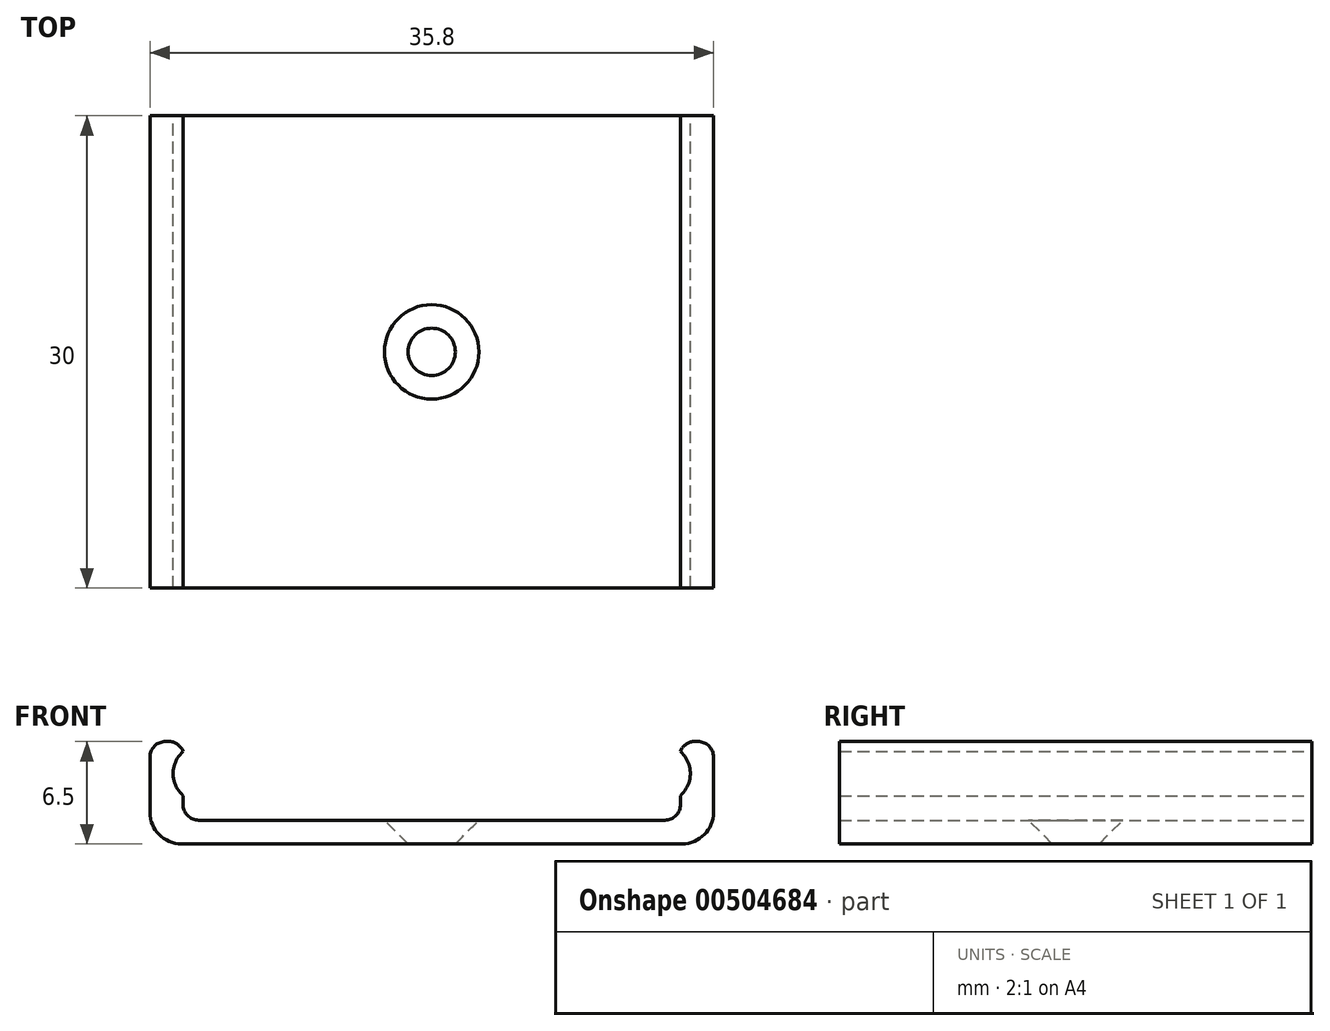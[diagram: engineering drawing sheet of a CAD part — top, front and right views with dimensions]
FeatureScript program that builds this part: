
annotation { "Feature Type Name" : "Feature", "Feature Type Description" : "" }
export const myFeature = defineFeature(function(context is Context, id is Id, definition is map)
    precondition{}
    {
        {
            var Q0;
            Q0=qCreatedBy(makeId("Front.planeOp"),FACE);
            var sketch = newSketch(context, id + "F0", { "sketchPlane" : qUnion([Q0])});
            skLineSegment(sketch, "E0", {"start": v(-17.9, 0) * mm, "end": v(17.9, 0) * mm});
            skLineSegment(sketch, "E1", {"start": v(-16.4, 15.5) * mm, "end": v(-16.4, -15.28) * mm, "construction": true});
            skLineSegment(sketch, "E2", {"start": v(16.4, 15.5) * mm, "end": v(16.4, -15.28) * mm, "construction": true});
            skLineSegment(sketch, "E3", {"start": v(15.8, 1.5) * mm, "end": v(8, 1.5) * mm});
            skLineSegment(sketch, "E4", {"start": v(0, 15.5) * mm, "end": v(0, -15.28) * mm, "construction": true});
            skLineSegment(sketch, "E5.trimOffspring", {"start": v(-8, 1.5) * mm, "end": v(-15.8, 1.5) * mm});
            skLineSegment(sketch, "E6", {"start": v(-17.9, 6.5) * mm, "end": v(-15.8, 6.5) * mm});
            skLineSegment(sketch, "E7", {"start": v(-15.8, 6.5) * mm, "end": v(-15.8, 1.5) * mm});
            skLineSegment(sketch, "E8", {"start": v(17.9, 6.5) * mm, "end": v(15.8, 6.5) * mm});
            skLineSegment(sketch, "E9", {"start": v(15.8, 6.5) * mm, "end": v(15.8, 1.5) * mm});
            skLineSegment(sketch, "E10", {"start": v(17.9, 6.5) * mm, "end": v(17.9, 0) * mm});
            skLineSegment(sketch, "E11", {"start": v(-17.9, 6.5) * mm, "end": v(-17.9, 0) * mm});
            skEllipse(sketch, "E12", {"center": v(12.93, 4.47) * mm, "majorRadius": 3.5 * mm, "minorRadius": 2.48 * mm, "majorAxis": v(-1, 0)});
            skEllipse(sketch, "E13", {"center": v(-12.93, 4.47) * mm, "majorRadius": 3.5 * mm, "minorRadius": 2.48 * mm, "majorAxis": v(-1, 0)});
            skLineSegment(sketch, "E14", {"start": v(-8, 1.5) * mm, "end": v(8, 1.5) * mm});
            skSolve(sketch);
        }
        {
            var Q0;
            Q0=qSketchRegion(id+"F0",true);
            extrude(context, id + "F1", {"entities" : qUnion([Q0]), "depth" : 30 * mm});
        }
        {
            var Q0;
            Q0=makeQuery(id+"F1.opExtrude","SWEPT_FACE",FACE,{"disambiguationData":[OSD([sQuery(id+"F0.wireOp",EDGE,"E3"),sQuery(id+"F0.wireOp",EDGE,"E5.trimOffspring"),sQuery(id+"F0.wireOp",EDGE,"E14")])]});
            var sketch = newSketch(context, id + "F2", { "sketchPlane" : qUnion([Q0])});
            skLineSegment(sketch, "E15", {"start": v(0, -30) * mm, "end": v(0, 0) * mm, "construction": true});
            skLineSegment(sketch, "E16", {"start": v(15.8, -15) * mm, "end": v(-15.8, -15) * mm, "construction": true});
            skCircle(sketch, "E17", {"center": v(0, -15) * mm, "radius": 3 * mm});
            skSolve(sketch);
        }
        {
            var Q0;
            Q0=sQuery(id+"F2.wireOp",VERTEX,"E17.center");
            var Q1;
            Q1=makeQuery(id+"F1.opExtrude","SWEPT_BODY",BODY,{"disambiguationData":[OSD([sQuery(id+"F0.wireOp",EDGE,"E0"),sQuery(id+"F0.wireOp",EDGE,"E3"),sQuery(id+"F0.wireOp",EDGE,"D1xSTUMQ-20cp-QuWq-AnQI-jtTS1Aydl4wU"),sQuery(id+"F0.wireOp",EDGE,"RWH1BVH5-31CH-0wRi-MlRQ-n6gno6U9d2sJ"),sQuery(id+"F0.wireOp",EDGE,"HIeZi0eG-o20j-5PzK-DNVY-zvFXTWfz9iDB"),sQuery(id+"F0.wireOp",EDGE,"E5.trimOffspring"),sQuery(id+"F0.wireOp",EDGE,"E6"),sQuery(id+"F0.wireOp",EDGE,"E7"),sQuery(id+"F0.wireOp",EDGE,"E8"),sQuery(id+"F0.wireOp",EDGE,"E9"),sQuery(id+"F0.wireOp",EDGE,"E10"),sQuery(id+"F0.wireOp",EDGE,"E11")])]});
            hole(context, id + "F3", {"style" : HoleStyle.C_SINK, "endStyle" : HoleEndStyle.THROUGH, "holeDiameter" : 3 * mm, "cSinkDiameter" : 6 * mm, "cSinkAngle" : 90 * degree, "isTappedThrough" : true, "tappedDepth" : 12 * mm, "tapClearance" : 3, "locations" : qUnion([Q0]), "scope" : qUnion([Q1]), "majorDiameter" : 5 * mm});
        }
        {
            var Q0;
            {var subQ0=sQuery(id+"F0.wireOp",EDGE,"E12");var subQ1=sQuery(id+"F0.wireOp",EDGE,"E9");var subQ2=makeQuery(id+"F0.imprint","INTERSECT",VERTEX,{"disambiguationData":[OD(0.0)],"derivedFrom":[subQ1,subQ0]});Q0=makeQuery(id+"F0.imprint","IMPRINT",FACE,{"disambiguationData":[TD([[makeQuery(id+"F0.imprint","IMPRINT",EDGE,{"disambiguationData":[TD([[subQ2,-1.0]])],"derivedFrom":subQ1}),-1.0]])]});}
            var Q1;
            {var subQ0=sQuery(id+"F0.wireOp",EDGE,"E12");var subQ1=sQuery(id+"F0.wireOp",EDGE,"E9");var subQ2=makeQuery(id+"F0.imprint","INTERSECT",VERTEX,{"disambiguationData":[OD(0.0)],"derivedFrom":[subQ1,subQ0]});Q1=makeQuery(id+"F0.imprint","IMPRINT",FACE,{"disambiguationData":[TD([[makeQuery(id+"F0.imprint","IMPRINT",EDGE,{"disambiguationData":[TD([[subQ2,-1.0]])],"derivedFrom":subQ1}),1.0]])]});}
            var Q2;
            {var subQ0=sQuery(id+"F0.wireOp",EDGE,"E13");var subQ1=sQuery(id+"F0.wireOp",EDGE,"E7");var subQ2=makeQuery(id+"F0.imprint","INTERSECT",VERTEX,{"disambiguationData":[OD(0.0)],"derivedFrom":[subQ1,subQ0]});Q2=makeQuery(id+"F0.imprint","IMPRINT",FACE,{"disambiguationData":[TD([[makeQuery(id+"F0.imprint","IMPRINT",EDGE,{"disambiguationData":[TD([[subQ2,-1.0]])],"derivedFrom":subQ1}),1.0]])]});}
            var Q3;
            {var subQ0=sQuery(id+"F0.wireOp",EDGE,"E13");var subQ1=sQuery(id+"F0.wireOp",EDGE,"E7");var subQ2=makeQuery(id+"F0.imprint","INTERSECT",VERTEX,{"disambiguationData":[OD(0.0)],"derivedFrom":[subQ1,subQ0]});Q3=makeQuery(id+"F0.imprint","IMPRINT",FACE,{"disambiguationData":[TD([[makeQuery(id+"F0.imprint","IMPRINT",EDGE,{"disambiguationData":[TD([[subQ2,-1.0]])],"derivedFrom":subQ1}),-1.0]])]});}
            var Q4;
            Q4=sQuery(id+"F0.wireOp",EDGE,"E12");
            extrude(context, id + "F4", {"entities" : qUnion([Q0, Q1, Q2, Q3]), "operationType" : NewBodyOperationType.REMOVE, "surfaceEntities" : qUnion([Q4]), "endBound" : BoundingType.THROUGH_ALL, "depth" : 25 * mm});
        }
        {
            var Q0;
            Q0=makeQuery(id+"F1.opExtrude","SWEPT_EDGE",EDGE,{"disambiguationData":[OSD([sQuery(id+"F0.wireOp",EDGE,"E6"),sQuery(id+"F0.wireOp",EDGE,"E11")])]});
            var Q1;
            Q1=makeQuery(id+"F1.opExtrude","SWEPT_EDGE",EDGE,{"disambiguationData":[OSD([sQuery(id+"F0.wireOp",EDGE,"E8"),sQuery(id+"F0.wireOp",EDGE,"E10")])]});
            var Q2;
            Q2=makeQuery(id+"F1.opExtrude","SWEPT_EDGE",EDGE,{"disambiguationData":[OSD([sQuery(id+"F0.wireOp",EDGE,"E6"),sQuery(id+"F0.wireOp",EDGE,"E7")])]});
            var Q3;
            Q3=makeQuery(id+"F1.opExtrude","SWEPT_EDGE",EDGE,{"disambiguationData":[OSD([sQuery(id+"F0.wireOp",EDGE,"E8"),sQuery(id+"F0.wireOp",EDGE,"E9")])]});
            fillet(context, id + "F5", {"entities" : qUnion([Q0, Q1, Q2, Q3]), "radius" : 1 * mm, "tangentPropagation" : true, "allowEdgeOverflow" : false});
        }
        {
            var Q0;
            Q0=makeQuery(id+"F1.opExtrude","SWEPT_EDGE",EDGE,{"disambiguationData":[OSD([sQuery(id+"F0.wireOp",EDGE,"E5.trimOffspring"),sQuery(id+"F0.wireOp",EDGE,"E7")])]});
            var Q1;
            Q1=makeQuery(id+"F1.opExtrude","SWEPT_EDGE",EDGE,{"disambiguationData":[OSD([sQuery(id+"F0.wireOp",EDGE,"E3"),sQuery(id+"F0.wireOp",EDGE,"E9")])]});
            fillet(context, id + "F6", {"entities" : qUnion([Q0, Q1]), "radius" : 1 * mm, "tangentPropagation" : true, "allowEdgeOverflow" : false});
        }
        {
            var Q0;
            Q0=makeQuery(id+"F1.opExtrude","SWEPT_EDGE",EDGE,{"disambiguationData":[OSD([sQuery(id+"F0.wireOp",EDGE,"E0"),sQuery(id+"F0.wireOp",EDGE,"E11")])]});
            var Q1;
            Q1=makeQuery(id+"F1.opExtrude","SWEPT_EDGE",EDGE,{"disambiguationData":[OSD([sQuery(id+"F0.wireOp",EDGE,"E0"),sQuery(id+"F0.wireOp",EDGE,"E10")])]});
            fillet(context, id + "F7", {"entities" : qUnion([Q0, Q1]), "radius" : 2 * mm, "tangentPropagation" : true, "allowEdgeOverflow" : false});
        }
    });
